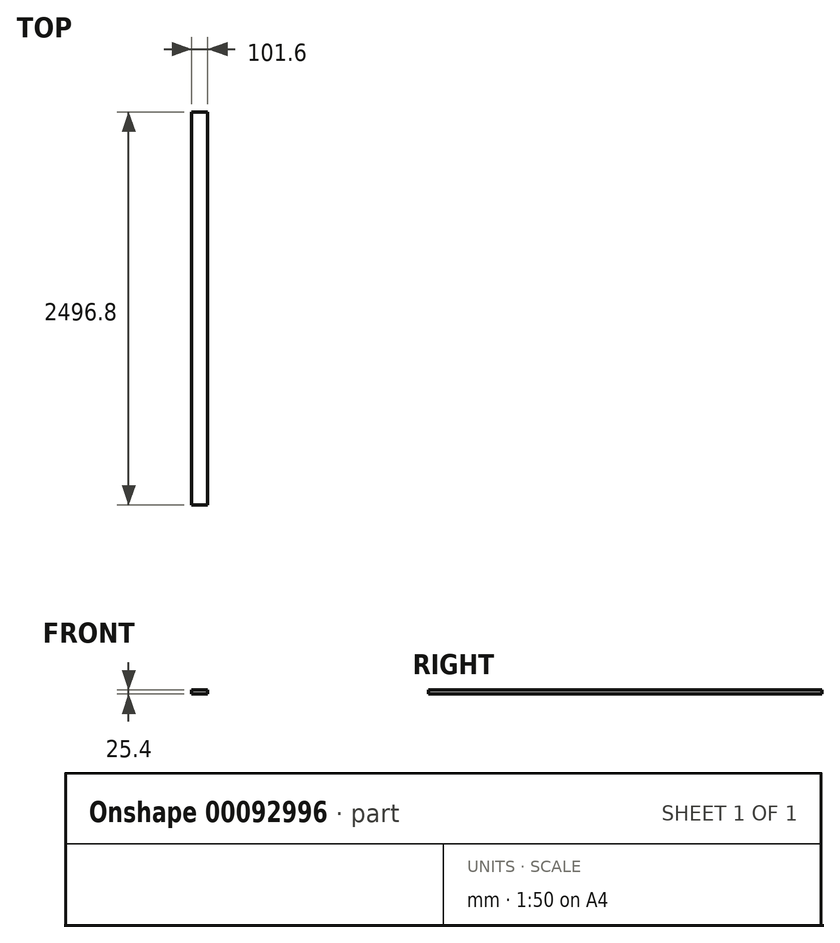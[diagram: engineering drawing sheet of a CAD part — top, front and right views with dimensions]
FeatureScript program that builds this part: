
annotation { "Feature Type Name" : "Feature", "Feature Type Description" : "" }
export const myFeature = defineFeature(function(context is Context, id is Id, definition is map)
    precondition{}
    {
        {
            var Q0;
            Q0=qCreatedBy(makeId("Front.planeOp"),FACE);
            var sketch = newSketch(context, id + "F0", { "sketchPlane" : qUnion([Q0])});
            skLineSegment(sketch, "E0.bottom", {"start": v(-50.8, 25.4) * mm, "end": v(50.8, 25.4) * mm});
            skLineSegment(sketch, "E0.top", {"start": v(-50.8, 0) * mm, "end": v(50.8, 0) * mm});
            skLineSegment(sketch, "E0.left", {"start": v(-50.8, 25.4) * mm, "end": v(-50.8, 0) * mm});
            skLineSegment(sketch, "E0.right", {"start": v(50.8, 25.4) * mm, "end": v(50.8, 0) * mm});
            skSolve(sketch);
        }
        {
            var Q0;
            Q0=qSketchRegion(id+"F0",true);
            var Q1;
            Q1=makeQuery(id+"F0.imprint","IMPRINT",FACE,{"disambiguationData":[TD([[makeQuery(id+"F0.imprint","IMPRINT",EDGE,{"derivedFrom":sQuery(id+"F0.wireOp",EDGE,"E0.bottom")}),-1.0]])]});
            extrude(context, id + "F1", {"entities" : qUnion([Q0, Q1]), "oppositeDirection" : true, "depth" : 2496.8 * mm});
        }
    });
